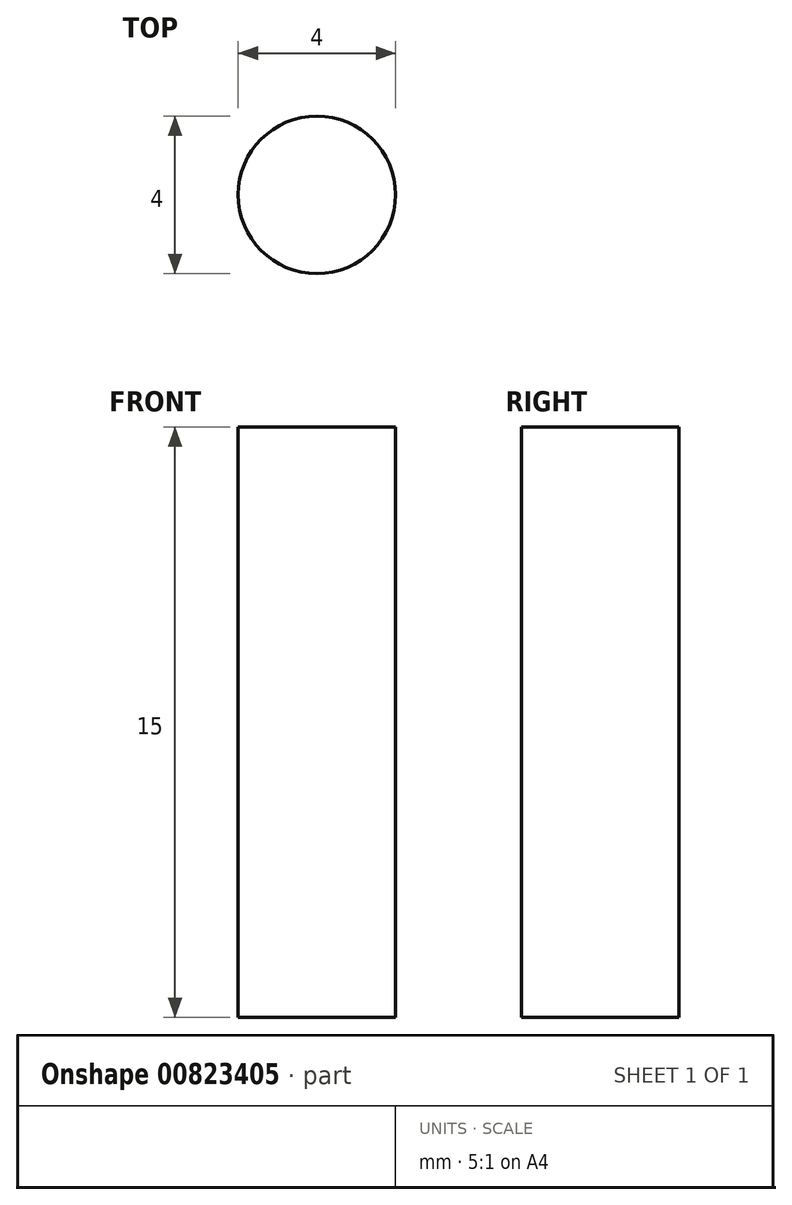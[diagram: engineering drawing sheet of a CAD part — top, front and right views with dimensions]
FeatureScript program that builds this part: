
annotation { "Feature Type Name" : "Feature", "Feature Type Description" : "" }
export const myFeature = defineFeature(function(context is Context, id is Id, definition is map)
    precondition{}
    {
        {
            var Q0;
            Q0=qCreatedBy(makeId("Top.planeOp"),FACE);
            var sketch = newSketch(context, id + "F0", { "sketchPlane" : qUnion([Q0])});
            skCircle(sketch, "E0", {"center": v(0, 0) * mm, "radius": 2 * mm});
            skSolve(sketch);
        }
        {
            var Q0;
            Q0 = qSketchRegion(id + "F0", true);
            extrude(context, id + "F1", {"entities" : qUnion([Q0]), "depth" : 15 * mm, "offsetDistance" : 25 * mm});
        }
    });
